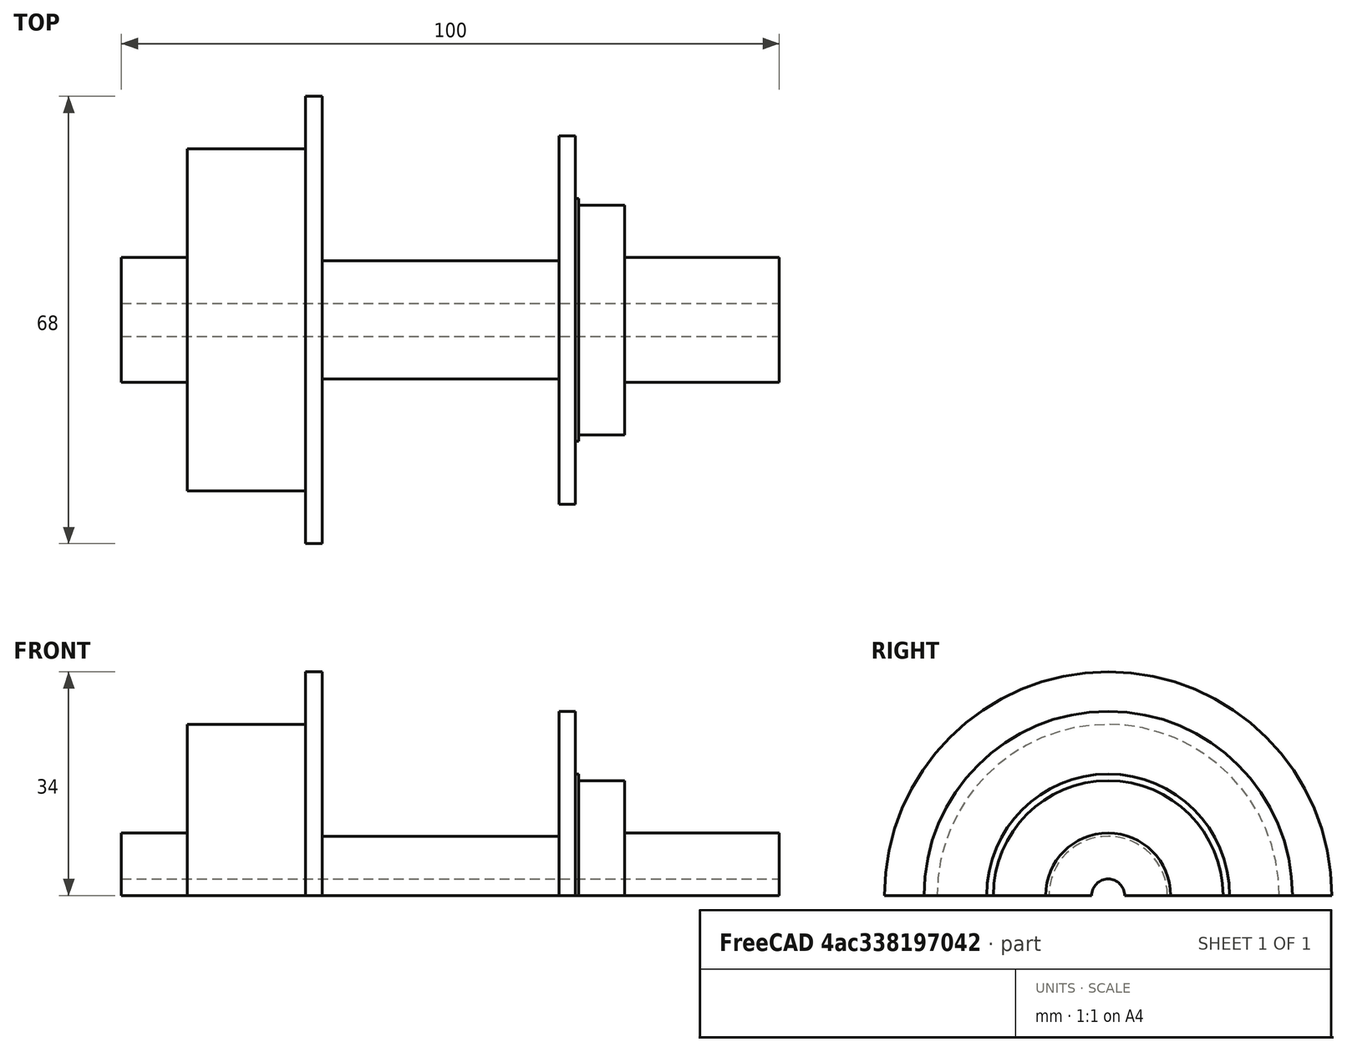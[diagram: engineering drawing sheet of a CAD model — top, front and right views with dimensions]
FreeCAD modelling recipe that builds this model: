
FCSTD DOCUMENT  (FreeCAD 0.16R)
Label: 100mmMTB_wChainline50mmtire_V1
License: All rights reserved
LicenseURL: http://en.wikipedia.org/wiki/All_rights_reserved
objects: Sketcher::SketchObject×1, PartDesign::Revolution×1
note: 3 computed .brp shape members not serialized (recipe doc carries the construction recipe); baked Part::Feature solids carry a one-line shape summary decoded from their .brp

FEATURE [Sketcher::SketchObject] Sketch
  sketch-geometry (87):
    g0: LineSegment StartX=26.5 StartY=9.5 StartZ=0 EndX=26.5 EndY=17.46 EndZ=0
    g1: LineSegment StartX=26.5 StartY=17.46 StartZ=0 EndX=19.5 EndY=17.46 EndZ=0
    g2: LineSegment StartX=19.5 StartY=18.46 StartZ=0 EndX=19 EndY=18.46 EndZ=0
    g3: LineSegment StartX=19 StartY=18.46 StartZ=0 EndX=19 EndY=28 EndZ=0
    g4: LineSegment StartX=19 StartY=28 StartZ=0 EndX=16.5 EndY=28 EndZ=0
    g5: LineSegment StartX=16.5 StartY=28 StartZ=0 EndX=16.5 EndY=9 EndZ=0
    g6: LineSegment StartX=16.5 StartY=9 StartZ=0 EndX=-19.5 EndY=9 EndZ=0
    g7: LineSegment StartX=-19.5 StartY=9 StartZ=0 EndX=-19.5 EndY=34 EndZ=0
    g8: LineSegment StartX=-19.5 StartY=34 StartZ=0 EndX=-22 EndY=34 EndZ=0
    g9: LineSegment StartX=-22 StartY=34 StartZ=0 EndX=-22 EndY=26 EndZ=0
    g10: LineSegment StartX=-40 StartY=26 StartZ=0 EndX=-40 EndY=9.5 EndZ=0
    g11: LineSegment StartX=19.5 StartY=18.46 StartZ=0 EndX=19.5 EndY=17.46 EndZ=0
    g12: LineSegment StartX=-40 StartY=26 StartZ=0 EndX=-22 EndY=26 EndZ=0
    g13: LineSegment [constr] StartX=22 StartY=55 StartZ=0 EndX=22 EndY=0 EndZ=0
    g14: LineSegment [constr] StartX=27.5 StartY=45 StartZ=0 EndX=27.5 EndY=20 EndZ=0
    g15: LineSegment [constr] StartX=33 StartY=33 StartZ=0 EndX=33 EndY=20 EndZ=0
    g16: LineSegment [constr] StartX=38.5 StartY=28 StartZ=0 EndX=38.5 EndY=20 EndZ=0
    g17: LineSegment [constr] StartX=44 StartY=22.5 StartZ=0 EndX=44 EndY=9.5 EndZ=0
    g18: LineSegment StartX=-50 StartY=2.5 StartZ=0 EndX=-50 EndY=9.5 EndZ=0
    g19: LineSegment [constr] StartX=-41.6 StartY=60 StartZ=0 EndX=-40 EndY=60 EndZ=0
    g20: LineSegment [constr] StartX=-40 StartY=60 StartZ=0 EndX=-40 EndY=20 EndZ=0
    g21: LineSegment [constr] StartX=-40 StartY=20 StartZ=0 EndX=-41.6 EndY=20 EndZ=0
    g22: LineSegment [constr] StartX=-41.6 StartY=20 StartZ=0 EndX=-41.6 EndY=60 EndZ=0
    g23: LineSegment [constr] StartX=0 StartY=0 StartZ=0 EndX=0 EndY=193 EndZ=0
    g24: LineSegment [constr] StartX=-22 StartY=34 StartZ=0 EndX=0 EndY=193 EndZ=0
    g25: LineSegment [constr] StartX=19 StartY=28 StartZ=0 EndX=0 EndY=193 EndZ=0
    g26: LineSegment StartX=26.5 StartY=9.5 StartZ=0 EndX=50 EndY=9.5 EndZ=0
    g27: LineSegment StartX=50 StartY=9.5 StartZ=0 EndX=50 EndY=2.5 EndZ=0
    g28: LineSegment StartX=-50 StartY=2.5 StartZ=0 EndX=50 EndY=2.5 EndZ=0
    g29: LineSegment StartX=-40 StartY=9.5 StartZ=0 EndX=-50 EndY=9.5 EndZ=0
    g30: Circle [constr] CenterX=0 CenterY=229 CenterZ=0 NormalX=0 NormalY=0 NormalZ=1 Radius=25
    g31: LineSegment [constr] StartX=-30 StartY=331 StartZ=0 EndX=30 EndY=331 EndZ=0
    g32: LineSegment [constr] StartX=30 StartY=299 StartZ=0 EndX=-30 EndY=299 EndZ=0
    g33: LineSegment [constr] StartX=-30 StartY=299 StartZ=0 EndX=-30 EndY=331 EndZ=0
    g34: LineSegment [constr] StartX=36 StartY=379 StartZ=0 EndX=33 EndY=379 EndZ=0
    g35: LineSegment [constr] StartX=33 StartY=379 StartZ=0 EndX=33 EndY=251 EndZ=0
    g36: LineSegment [constr] StartX=33 StartY=251 StartZ=0 EndX=36 EndY=251 EndZ=0
    g37: LineSegment [constr] StartX=30 StartY=331 StartZ=0 EndX=30 EndY=315 EndZ=0
    g38: LineSegment [constr] StartX=30 StartY=315 StartZ=0 EndX=30 EndY=299 EndZ=0
    g39: LineSegment [constr] StartX=36 StartY=379 StartZ=0 EndX=36 EndY=315 EndZ=0
    g40: LineSegment [constr] StartX=36 StartY=315 StartZ=0 EndX=36 EndY=251 EndZ=0
    g41: LineSegment [constr] StartX=30 StartY=315 StartZ=0 EndX=110 EndY=315 EndZ=0
    g42: LineSegment [constr] StartX=-40 StartY=60 StartZ=0 EndX=-40 EndY=42 EndZ=0
    g43: LineSegment [constr] StartX=-40 StartY=60 StartZ=0 EndX=-24 EndY=60 EndZ=0
    g44: LineSegment [constr] StartX=-24 StartY=60 StartZ=0 EndX=-24 EndY=42 EndZ=0
    g45: LineSegment [constr] StartX=-24 StartY=42 StartZ=0 EndX=-40 EndY=42 EndZ=0
    g46: LineSegment [constr] StartX=-25 StartY=254 StartZ=0 EndX=25 EndY=254 EndZ=0
    g47: LineSegment [constr] StartX=22 StartY=0 StartZ=0 EndX=36 EndY=315 EndZ=0
    g48: LineSegment [constr] StartX=29.1959 StartY=240.735 StartZ=0 EndX=27.738 EndY=207.933 EndZ=0
    g49: LineSegment [constr] StartX=34.5926 StartY=204.506 StartZ=0 EndX=33.1835 EndY=172.8 EndZ=0
    g50: LineSegment [constr] StartX=36 StartY=315 StartZ=0 EndX=36 EndY=-60.2245 EndZ=0
    g51: Circle [constr] CenterX=0 CenterY=229 CenterZ=0 NormalX=0 NormalY=0 NormalZ=1 Radius=31.75
    g52: Circle [constr] CenterX=0 CenterY=229 CenterZ=0 NormalX=0 NormalY=0 NormalZ=1 Radius=29.3
    g53: LineSegment [constr] StartX=-50 StartY=60.1818 StartZ=0 EndX=-53.2 EndY=60.1818 EndZ=0
    g54: LineSegment [constr] StartX=-53.2 StartY=60.1818 StartZ=0 EndX=-53.2 EndY=0.090679 EndZ=0
    g55: LineSegment [constr] StartX=-53.2 StartY=0.090679 StartZ=0 EndX=-50 EndY=0.090679 EndZ=0
    g56: LineSegment [constr] StartX=-50 StartY=0.090679 StartZ=0 EndX=-50 EndY=60.1818 EndZ=0
    g57: LineSegment [constr] StartX=-28.5943 StartY=215.201 StartZ=0 EndX=-50.0989 EndY=76.3177 EndZ=0
    g58: LineSegment [constr] StartX=-20.4484 StartY=202.457 StartZ=0 EndX=-39.927 EndY=76.6585 EndZ=0
    g59: LineSegment [constr] StartX=20.3595 StartY=203.492 StartZ=0 EndX=46.7509 EndY=48.3487 EndZ=0
    g60: LineSegment [constr] StartX=29.1431 StartY=211.487 StartZ=0 EndX=56.1775 EndY=52.564 EndZ=0
    g61: LineSegment [constr] StartX=50 StartY=54.306 StartZ=0 EndX=53.2 EndY=54.306 EndZ=0
    g62: LineSegment [constr] StartX=53.2 StartY=54.306 StartZ=0 EndX=53.2 EndY=-0.259602 EndZ=0
    g63: LineSegment [constr] StartX=53.2 StartY=-0.259602 StartZ=0 EndX=50 EndY=-0.259602 EndZ=0
    g64: LineSegment [constr] StartX=50 StartY=-0.259602 StartZ=0 EndX=50 EndY=54.306 EndZ=0
    g65: LineSegment [constr] StartX=42 StartY=315 StartZ=0 EndX=42 EndY=185 EndZ=0
    g66: LineSegment [constr] StartX=-44 StartY=315 StartZ=0 EndX=-44 EndY=185 EndZ=0
    g67: LineSegment [constr] StartX=-34.1217 StartY=94.0838 StartZ=0 EndX=-54.608 EndY=58.6006 EndZ=0
    g68: LineSegment [constr] StartX=-30.696 StartY=93.6173 StartZ=0 EndX=-50 EndY=60.1818 EndZ=0
    g69: Circle [constr] CenterX=0 CenterY=206.598 CenterZ=0 NormalX=0 NormalY=0 NormalZ=1 Radius=13.75
    g70: Circle [constr] CenterX=-55.5 CenterY=60.5 CenterZ=0 NormalX=0 NormalY=0 NormalZ=1 Radius=2.75
    g71: Circle [constr] CenterX=-55.5 CenterY=26.5 CenterZ=0 NormalX=0 NormalY=0 NormalZ=1 Radius=2.75
    g72: LineSegment [constr] StartX=-59.5 StartY=66.4736 StartZ=0 EndX=-49.5 EndY=66.4736 EndZ=0
    g73: LineSegment [constr] StartX=-49.5 StartY=66.4736 StartZ=0 EndX=-49.5 EndY=20.9721 EndZ=0
    g74: LineSegment [constr] StartX=-49.5 StartY=20.9721 StartZ=0 EndX=-59.5 EndY=20.9721 EndZ=0
    g75: LineSegment [constr] StartX=-59.5 StartY=20.9721 StartZ=0 EndX=-59.5 EndY=66.4736 EndZ=0
    g76: Circle [constr] CenterX=-53.5 CenterY=60.5 CenterZ=0 NormalX=0 NormalY=0 NormalZ=1 Radius=2.75
    g77: Circle [constr] CenterX=-53.5 CenterY=26.5 CenterZ=0 NormalX=0 NormalY=0 NormalZ=1 Radius=2.75
    g78: LineSegment [constr] StartX=-22.0773 StartY=40.7378 StartZ=0 EndX=-23.126 EndY=33.1585 EndZ=0
    g79: LineSegment [constr] StartX=-22 StartY=31 StartZ=0 EndX=-19.5 EndY=31 EndZ=0
    g80: LineSegment [constr] StartX=-19.5 StartY=31 StartZ=0 EndX=-19.5 EndY=28.9 EndZ=0
    g81: LineSegment [constr] StartX=-19.5 StartY=28.9 StartZ=0 EndX=-22 EndY=28.9 EndZ=0
    g82: LineSegment [constr] StartX=-22 StartY=28.9 StartZ=0 EndX=-22 EndY=31 EndZ=0
    g83: LineSegment [constr] StartX=16.5 StartY=22.4 StartZ=0 EndX=19 EndY=22.4 EndZ=0
    g84: LineSegment [constr] StartX=19 StartY=22.4 StartZ=0 EndX=19 EndY=24.5 EndZ=0
    g85: LineSegment [constr] StartX=19 StartY=24.5 StartZ=0 EndX=16.5 EndY=24.5 EndZ=0
    g86: LineSegment [constr] StartX=16.5 StartY=24.5 StartZ=0 EndX=16.5 EndY=22.4 EndZ=0
  constraints (245):
    c: Coincident(g2,g3)
    c: Vertical(g3)
    c: Coincident(g3,g4)
    c: Horizontal(g4)
    c: Coincident(g4,g5)
    c: Vertical(g5)
    c: Horizontal(g6)
    c: Vertical(g7)
    c: Coincident(g7,g8)
    c: Horizontal(g1)
    c: Horizontal(g8)
    c: DistanceY(g-1,g0) = 9.5
    c: Vertical(g0)
    c: DistanceX(g2,g2) = 0.5
    c: Horizontal(g2)
    c: DistanceY(g-1,g1) = 17.46
    c: DistanceX(g4,g4) = 2.5
    c: DistanceX(g1,g1) = 7
    c: DistanceY(g1,g2) = 1
    c: DistanceY(g-1,g6) = 9
    c: DistanceX(g8,g8) = 2.5
    c: DistanceY(g-1,g4) = 28
    c: Coincident(g8,g9)
    c: Vertical(g10)
    c: Vertical(g9)
    c: DistanceY(g8) = 34
    c: DistanceY(g10) = 26
    c: DistanceX(g10,g9) = 18
    c: Vertical(g11)
    c: Coincident(g11,g2)
    c: Coincident(g11,g1)
    c: Horizontal(g12)
    c: Coincident(g12,g10)
    c: Coincident(g12,g9)
    c: Vertical(g13)
    c: Vertical(g14)
    c: Vertical(g15)
    c: Vertical(g17)
    c: Vertical(g16)
    c: DistanceX(g13,g14) = 5.5
    c: DistanceX(g14,g15) = 5.5
    c: DistanceX(g15,g16) = 5.5
    c: DistanceX(g16,g17) = 5.5
    c: DistanceY(g13) = 55
    c: DistanceX(g2,g13) = 3
    c: Vertical(g18)
    c: Coincident(g19,g20)
    c: Coincident(g20,g21)
    c: Coincident(g21,g22)
    c: Coincident(g22,g19)
    c: Horizontal(g19)
    c: Horizontal(g21)
    c: Vertical(g20)
    c: Vertical(g22)
    c: DistanceX(g19,g19) = 1.6
    c: PointOnObject(g23,g-1)
    c: Vertical(g23)
    c: Distance(g23) = 193
    c: Coincident(g24,g23)
    c: Coincident(g24,g25)
    c: Coincident(g25,g3)
    c: Coincident(g24,g8)
    c: DistanceY(g16) = 20
    c: DistanceY(g15) = 20
    c: DistanceY(g14) = 20
    c: Distance(g14) = 25
    c: Distance(g16) = 8
    c: Distance(g15) = 13
    c: DistanceY(g17,g17) = 13
    c: Coincident(g1,g0)
    c: Coincident(g28,g27)
    c: Horizontal(g28)
    c: Vertical(g27)
    c: Distance(g26,g17) = 6
    c: Coincident(g27,g26)
    c: PointOnObject(g17,g26)
    c: Horizontal(g26)
    c: DistanceY(g26) = 9.5
    c: DistanceY(g27) = 2.5
    c: DistanceX(g18,g27) = 100
    c: DistanceX(g18,g23) = 50
    c: Coincident(g29,g10)
    c: Coincident(g29,g18)
    c: DistanceY(g20) = 20
    c: Coincident(g18,g28)
    c: Horizontal(g29)
    c: DistanceY(g10) = 9.5
    c: PointOnObject(g20,g10)
    c: DistanceX(g29,g29) = 10
    c: Coincident(g26,g0)
    c: Coincident(g-1,g23)
    c: Radius(g30) = 25
    c: PointOnObject(g30,g-2)
    c: Coincident(g32,g33)
    c: Coincident(g33,g31)
    c: Horizontal(g31)
    c: Horizontal(g32)
    c: Vertical(g33)
    c: Symmetric(g32,g32,g-2)
    c: Distance(g31) = 60
    c: Coincident(g34,g35)
    c: Coincident(g35,g36)
    c: Horizontal(g34)
    c: Horizontal(g36)
    c: Vertical(g35)
    c: Distance(g36) = 3
    c: Distance(g35) = 128
    c: Vertical(g37)
    c: Coincident(g38,g37)
    c: Coincident(g37,g31)
    c: Coincident(g38,g32)
    c: Symmetric(g31,g32,g37)
    c: Vertical(g39)
    c: Coincident(g40,g36)
    c: Coincident(g39,g34)
    c: Vertical(g40)
    c: Coincident(g40,g39)
    c: Horizontal(g41)
    c: Coincident(g41,g37)
    c: Distance(g41) = 80
    c: PointOnObject(g39,g41)
    c: DistanceX(g37,g39) = 6
    c: Vertical(g42)
    c: Horizontal(g43)
    c: Coincident(g43,g44)
    c: Coincident(g44,g45)
    c: Coincident(g45,g42)
    c: Horizontal(g45)
    c: Vertical(g44)
    c: Distance(g45) = 16
    c: Coincident(g43,g42)
    c: Distance(g44) = 18
    c: PointOnObject(g42,g20)
    c: Coincident(g42,g19)
    c: DistanceY(g19) = 60
    c: DistanceY(g37) = 315
    c: Distance(g33) = 32
    c: Symmetric(g36,g34,g41)
    c: Tangent(g46,g30)
    c: Horizontal(g46)
    c: Symmetric(g46,g46,g-2)
    c: DistanceY(g-1,g46) = 254
    c: PointOnObject(g13,g-1)
    c: Coincident(g47,g13)
    c: Coincident(g47,g39)
    c: Distance(g46) = 50
    c: Parallel(g48,g47)
    c: Parallel(g49,g47)
    c: Distance(g48,g47) = 3.5
    c: Distance(g49,g47) = 3.5
    c: Coincident(g50,g39)
    c: Vertical(g50)
    c: Radius(g51) = 31.75
    c: Coincident(g51,g30)
    c: Coincident(g52,g30)
    c: Radius(g52) = 29.3
    c: Coincident(g53,g54)
    c: Coincident(g54,g55)
    c: Coincident(g55,g56)
    c: Coincident(g56,g53)
    c: Horizontal(g53)
    c: Horizontal(g55)
    c: Vertical(g54)
    c: Vertical(g56)
    c: Distance(g55) = 3.2
    c: PointOnObject(g18,g56)
    c: PointOnObject(g57,g51)
    c: Distance(g58,g57) = 10
    c: Parallel(g58,g57)
    c: Distance(g60,g59) = 10
    c: Parallel(g60,g59)
    c: Coincident(g61,g62)
    c: Coincident(g62,g63)
    c: Coincident(g63,g64)
    c: Coincident(g64,g61)
    c: Horizontal(g61)
    c: Horizontal(g63)
    c: Vertical(g62)
    c: Vertical(g64)
    c: Distance(g61) = 3.2
    c: PointOnObject(g26,g64)
    c: Vertical(g65)
    c: Distance(g65) = 130
    c: PointOnObject(g65,g41)
    c: Distance(g65,g39) = 6
    c: Vertical(g66)
    c: Distance(g66) = 130
    c: PointOnObject(g66,g41)
    c: Distance(g66,g33) = 14
    c: Distance(g67,g68) = 3.2
    c: Parallel(g68,g67)
    c: Coincident(g68,g53)
    c: Angle(g67) = -2.0944
    c: Radius(g69) = 13.75
    c: PointOnObject(g69,g23)
    c: Radius(g70) = 2.75
    c: Equal(g70,g71)
    c: Distance(g70,g71) = 34
    c: Coincident(g72,g73)
    c: Coincident(g73,g74)
    c: Coincident(g74,g75)
    c: Coincident(g75,g72)
    c: Horizontal(g72)
    c: Horizontal(g74)
    c: Vertical(g73)
    c: Vertical(g75)
    c: Distance(g74) = 10
    c: Distance(g70,g75) = 4
    c: DistanceY(g-1,g71) = 26.5
    c: Radius(g77) = 2.75
    c: Equal(g77,g76)
    c: DistanceY(g77) = 26.5
    c: Distance(g76,g77) = 34
    c: Distance(g76,g73) = 4
    c: Distance(g77,g73) = 4
    c: Distance(g77,g20) = 13.5
    c: Parallel(g78,g24)
    c: Distance(g78,g24) = 1
    c: Coincident(g6,g7)
    c: Coincident(g5,g6)
    c: Distance(g77,g71) = 2
    c: Coincident(g79,g80)
    c: Coincident(g80,g81)
    c: Coincident(g81,g82)
    c: Coincident(g82,g79)
    c: Horizontal(g79)
    c: Horizontal(g81)
    c: Vertical(g80)
    c: Vertical(g82)
    c: Distance(g80) = 2.1
    c: PointOnObject(g79,g9)
    c: PointOnObject(g79,g7)
    c: Distance(g79,g7) = 3
    c: Coincident(g83,g84)
    c: Coincident(g84,g85)
    c: Coincident(g85,g86)
    c: Coincident(g86,g83)
    c: Horizontal(g83)
    c: Horizontal(g85)
    c: Vertical(g84)
    c: Vertical(g86)
    c: PointOnObject(g84,g3)
    c: Distance(g86) = 2.1
    c: PointOnObject(g85,g5)
    c: Distance(g84,g3) = 3.5
FEATURE [PartDesign::Revolution] Revolution
  Angle = 180
  Axis = (1,0,0)
  Base = (0,0,0)
  ReferenceAxis = -> Sketch [H_Axis]
  Sketch = -> Sketch
